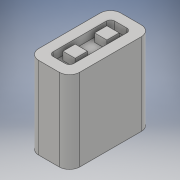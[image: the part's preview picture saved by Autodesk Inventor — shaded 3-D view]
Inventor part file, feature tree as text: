
AUTODESK INVENTOR PART (.ipt)
format: ipt  version: 2018 (Build 220112000, 112)  size: 186,880 bytes
history: native  units: in
note: dims shown in document units (in); Inventor stores cm internally (conversion verified against a paired STEP export)
features: sketch x8, extrude x6, fillet x4
ambient origin geometry x8: Origin, YZ Plane, XZ Plane, XY Plane, X Axis, Y Axis, Z Axis, Center Point
bodies: Solid1 (feature_tree)
feature tree (18):
  extrude  "Extrusion1"  Depth=1.0in
  fillet  "Fillet1"  Radius=1.0in
  extrude  "Extrusion2"  Depth=0.25in
  fillet  "Fillet2"  Radius=0.75in
  fillet  "Fillet3"  Radius=0.1in
  extrude  "Extrusion4"  Depth=0.25in TaperAngle=0.0deg
  sketch  "Sketch8"  dims[d20=0.1in d21=0.0in]
  sketch  "Sketch9"  dims[d22=0.15in d23=0.15in d24=0.15in d25=0.15in d27=0.0in d28=0.1in d29=0.5in]
  extrude  "Extrusion6"  Depth=0.15in
  fillet  "Fillet4"  Radius=0.15in
  sketch  "Sketch2"  dims[d0=0.5in d1=1.0in d2=1.0in d3=0.0in]
  sketch  "Sketch3"  dims[d4=0.125in d5=0.25in d6=0.75in d7=0.1in d8=0.0in]
  sketch  "Sketch6"  dims[d15=0.05in d16=0.15in d17=0.15in]
  sketch  "Sketch10"  dims[d30=0.4in d31=0.0in d32=0.05in]
  sketch  "Sketch4"  dims[d9=0.06in d10=0.25in d11=0.75in d13=0.0in d14=0.1in]
  sketch  "Sketch7"  dims[d18=0.15in d19=0.15in]
  extrude  "Extrusion3"  Depth=0.15in
  extrude  "Extrusion5"  Depth=0.5in
